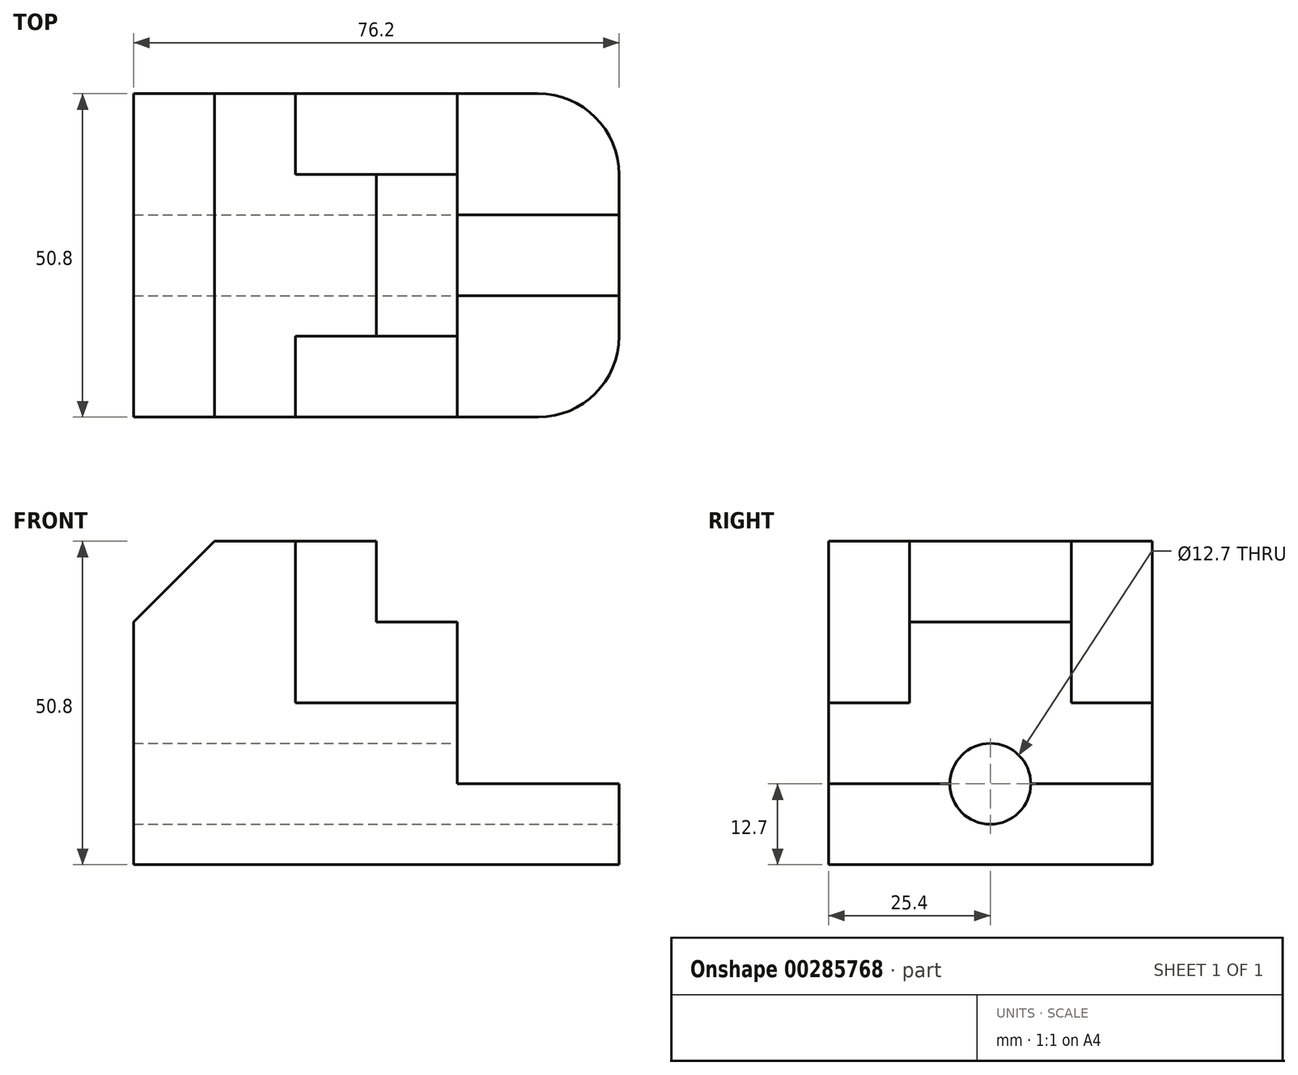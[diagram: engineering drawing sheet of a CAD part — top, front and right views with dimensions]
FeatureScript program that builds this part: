
annotation { "Feature Type Name" : "Feature", "Feature Type Description" : "" }
export const myFeature = defineFeature(function(context is Context, id is Id, definition is map)
    precondition{}
    {
        {
            var Q0;
            Q0=qCreatedBy(makeId("Front.planeOp"),FACE);
            var sketch = newSketch(context, id + "F0", { "sketchPlane" : qUnion([Q0])});
            skLineSegment(sketch, "E0.bottom", {"start": v(0, 0) * mm, "end": v(76.2, 0) * mm});
            skLineSegment(sketch, "E0.top", {"start": v(0, 50.8) * mm, "end": v(76.2, 50.8) * mm});
            skLineSegment(sketch, "E0.left", {"start": v(0, 0) * mm, "end": v(0, 50.8) * mm});
            skLineSegment(sketch, "E0.right", {"start": v(76.2, 0) * mm, "end": v(76.2, 50.8) * mm});
            skSolve(sketch);
        }
        {
            var Q0;
            Q0 = qSketchRegion(id + "F0", true);
            extrude(context, id + "F1", {"entities" : qUnion([Q0]), "endBound" : BoundingType.SYMMETRIC, "depth" : 50.8 * mm});
        }
        {
            var Q0;
            Q0=qCreatedBy(makeId("Front.planeOp"),FACE);
            var sketch = newSketch(context, id + "F2", { "sketchPlane" : qUnion([Q0])});
            skLineSegment(sketch, "E1", {"start": v(0, 50.8) * mm, "end": v(12.7, 50.8) * mm});
            skLineSegment(sketch, "E2", {"start": v(12.7, 50.8) * mm, "end": v(0, 38.1) * mm});
            skLineSegment(sketch, "E3", {"start": v(0, 38.1) * mm, "end": v(0, 50.8) * mm});
            skSolve(sketch);
        }
        {
            var Q0;
            Q0 = qSketchRegion(id + "F2", true);
            extrude(context, id + "F3", {"entities" : qUnion([Q0]), "operationType" : NewBodyOperationType.REMOVE, "endBound" : BoundingType.SYMMETRIC, "depth" : 50.8 * mm});
        }
        {
            var Q0;
            Q0=makeQuery(id+"F1.opExtrude","SWEPT_FACE",FACE,{"disambiguationData":[OSD([sQuery(id+"F0.wireOp",EDGE,"E0.right")])]});
            var sketch = newSketch(context, id + "F4", { "sketchPlane" : qUnion([Q0])});
            skLineSegment(sketch, "E4", {"start": v(-25.4, 12.7) * mm, "end": v(-6.35, 12.7) * mm});
            skLineSegment(sketch, "E5", {"start": v(25.4, 12.7) * mm, "end": v(6.35, 12.7) * mm});
            skArc(sketch, "E6", {"start": v(6.35, 12.7) * mm, "mid": v(0, 19.05) * mm, "end": v(-6.35, 12.7) * mm});
            skArc(sketch, "E7", {"start": v(-6.35, 12.7) * mm, "mid": v(0, 6.35) * mm, "end": v(6.35, 12.7) * mm});
            skLineSegment(sketch, "E8", {"start": v(-25.4, 12.7) * mm, "end": v(-25.4, 25.4) * mm});
            skLineSegment(sketch, "E9", {"start": v(-25.4, 25.4) * mm, "end": v(-12.7, 25.4) * mm});
            skLineSegment(sketch, "E10", {"start": v(-12.7, 25.4) * mm, "end": v(-12.7, 38.1) * mm});
            skLineSegment(sketch, "E11", {"start": v(-12.7, 38.1) * mm, "end": v(12.7, 38.1) * mm});
            skLineSegment(sketch, "E12", {"start": v(12.7, 38.1) * mm, "end": v(12.7, 25.4) * mm});
            skLineSegment(sketch, "E13", {"start": v(12.7, 25.4) * mm, "end": v(25.4, 25.4) * mm});
            skLineSegment(sketch, "E14", {"start": v(-25.4, 25.4) * mm, "end": v(-25.4, 12.7) * mm});
            skLineSegment(sketch, "E15", {"start": v(25.4, 25.4) * mm, "end": v(25.4, 12.7) * mm});
            skSolve(sketch);
        }
        {
            var Q0;
            Q0 = qSketchRegion(id + "F4", true);
            extrude(context, id + "F5", {"entities" : qUnion([Q0]), "operationType" : NewBodyOperationType.REMOVE, "depth" : 76.2 * mm});
        }
        {
            var Q0;
            Q0=makeQuery(id+"F4.imprint","IMPRINT",FACE,{"disambiguationData":[TD([[makeQuery(id+"F4.imprint","IMPRINT",EDGE,{"derivedFrom":sQuery(id+"F4.wireOp",EDGE,"E4")}),1.0]])]});
            extrude(context, id + "F6", {"entities" : qUnion([Q0]), "operationType" : NewBodyOperationType.REMOVE, "oppositeDirection" : true, "depth" : 25.4 * mm});
        }
        {
            var Q0;
            Q0=makeQuery(id+"F4.imprint","IMPRINT",FACE,{"disambiguationData":[TD([[makeQuery(id+"F4.imprint","IMPRINT",EDGE,{"derivedFrom":sQuery(id+"F4.wireOp",EDGE,"E6")}),1.0]])]});
            extrude(context, id + "F7", {"entities" : qUnion([Q0]), "operationType" : NewBodyOperationType.REMOVE, "oppositeDirection" : true, "depth" : 76.2 * mm});
        }
        {
            var Q0;
            Q0=makeQuery(id+"F1.opExtrude","CAP_FACE",FACE,{"disambiguationData":[OSD([sQuery(id+"F0.wireOp",EDGE,"E0.bottom"),sQuery(id+"F0.wireOp",EDGE,"E0.top"),sQuery(id+"F0.wireOp",EDGE,"E0.left"),sQuery(id+"F0.wireOp",EDGE,"E0.right")])],"isStart":false});
            var sketch = newSketch(context, id + "F8", { "sketchPlane" : qUnion([Q0])});
            skLineSegment(sketch, "E16", {"start": v(25.4, 50.8) * mm, "end": v(25.4, 25.4) * mm});
            skLineSegment(sketch, "E17", {"start": v(25.4, 25.4) * mm, "end": v(76.2, 25.4) * mm});
            skLineSegment(sketch, "E18", {"start": v(76.2, 25.4) * mm, "end": v(76.2, 50.8) * mm});
            skLineSegment(sketch, "E19", {"start": v(76.2, 50.8) * mm, "end": v(25.4, 50.8) * mm});
            skSolve(sketch);
        }
        {
            var Q0;
            Q0 = qSketchRegion(id + "F8", true);
            extrude(context, id + "F9", {"entities" : qUnion([Q0]), "operationType" : NewBodyOperationType.REMOVE, "oppositeDirection" : true, "depth" : 12.7 * mm});
        }
        {
            var Q0;
            Q0=makeQuery(id+"F1.opExtrude","CAP_FACE",FACE,{"disambiguationData":[OSD([sQuery(id+"F0.wireOp",EDGE,"E0.bottom"),sQuery(id+"F0.wireOp",EDGE,"E0.top"),sQuery(id+"F0.wireOp",EDGE,"E0.left"),sQuery(id+"F0.wireOp",EDGE,"E0.right")])],"isStart":true});
            var sketch = newSketch(context, id + "F10", { "sketchPlane" : qUnion([Q0])});
            skLineSegment(sketch, "E20.bottom", {"start": v(-76.2, 50.8) * mm, "end": v(-25.4, 50.8) * mm});
            skLineSegment(sketch, "E20.top", {"start": v(-76.2, 25.4) * mm, "end": v(-25.4, 25.4) * mm});
            skLineSegment(sketch, "E20.left", {"start": v(-76.2, 50.8) * mm, "end": v(-76.2, 25.4) * mm});
            skLineSegment(sketch, "E20.right", {"start": v(-25.4, 50.8) * mm, "end": v(-25.4, 25.4) * mm});
            skSolve(sketch);
        }
        {
            var Q0;
            Q0 = qSketchRegion(id + "F10", true);
            extrude(context, id + "F11", {"entities" : qUnion([Q0]), "operationType" : NewBodyOperationType.REMOVE, "oppositeDirection" : true, "depth" : 12.7 * mm});
        }
        {
            var Q0;
            {var subQ0=sQuery(id+"F0.wireOp",EDGE,"E0.top");var subQ1=sQuery(id+"F0.wireOp",EDGE,"E0.right");Q0=makeQuery(id+"F6.boolean.opBoolean","SPLIT",FACE,{"disambiguationData":[TD([makeQuery(id+"F1.opExtrude","SWEPT_FACE",FACE,{"disambiguationData":[OSD([subQ0])]})])],"derivedFrom":makeQuery(id+"F1.opExtrude","SWEPT_FACE",FACE,{"disambiguationData":[OSD([subQ1])]})});}
            var sketch = newSketch(context, id + "F12", { "sketchPlane" : qUnion([Q0])});
            skLineSegment(sketch, "E21.bottom", {"start": v(-12.7, 50.8) * mm, "end": v(12.7, 50.8) * mm});
            skLineSegment(sketch, "E21.top", {"start": v(-12.7, 38.1) * mm, "end": v(12.7, 38.1) * mm});
            skLineSegment(sketch, "E21.left", {"start": v(-12.7, 50.8) * mm, "end": v(-12.7, 38.1) * mm});
            skLineSegment(sketch, "E21.right", {"start": v(12.7, 50.8) * mm, "end": v(12.7, 38.1) * mm});
            skSolve(sketch);
        }
        {
            var Q0;
            Q0 = qSketchRegion(id + "F12", true);
            extrude(context, id + "F13", {"entities" : qUnion([Q0]), "operationType" : NewBodyOperationType.REMOVE, "oppositeDirection" : true, "depth" : 38.1 * mm});
        }
        {
            var Q0;
            {var subQ0=sQuery(id+"F0.wireOp",EDGE,"E0.bottom");var subQ1=sQuery(id+"F0.wireOp",EDGE,"E0.right");Q0=makeQuery(id+"F6.boolean.opBoolean","SPLIT",EDGE,{"disambiguationData":[TD([makeQuery(id+"F1.opExtrude","SWEPT_FACE",FACE,{"disambiguationData":[OSD([subQ0])]})])],"derivedFrom":makeQuery(id+"F1.opExtrude","CAP_EDGE",EDGE,{"disambiguationData":[OSD([subQ1])],"isStart":false})});}
            fillet(context, id + "F14", {"entities" : qUnion([Q0]), "radius" : 12.7 * mm, "tangentPropagation" : true, "allowEdgeOverflow" : false});
        }
        {
            var Q0;
            {var subQ0=sQuery(id+"F0.wireOp",EDGE,"E0.bottom");var subQ1=sQuery(id+"F0.wireOp",EDGE,"E0.right");Q0=makeQuery(id+"F6.boolean.opBoolean","SPLIT",EDGE,{"disambiguationData":[TD([makeQuery(id+"F1.opExtrude","SWEPT_FACE",FACE,{"disambiguationData":[OSD([subQ0])]})])],"derivedFrom":makeQuery(id+"F1.opExtrude","CAP_EDGE",EDGE,{"disambiguationData":[OSD([subQ1])],"isStart":true})});}
            fillet(context, id + "F15", {"entities" : qUnion([Q0]), "radius" : 12.7 * mm, "tangentPropagation" : true, "allowEdgeOverflow" : false});
        }
    });
